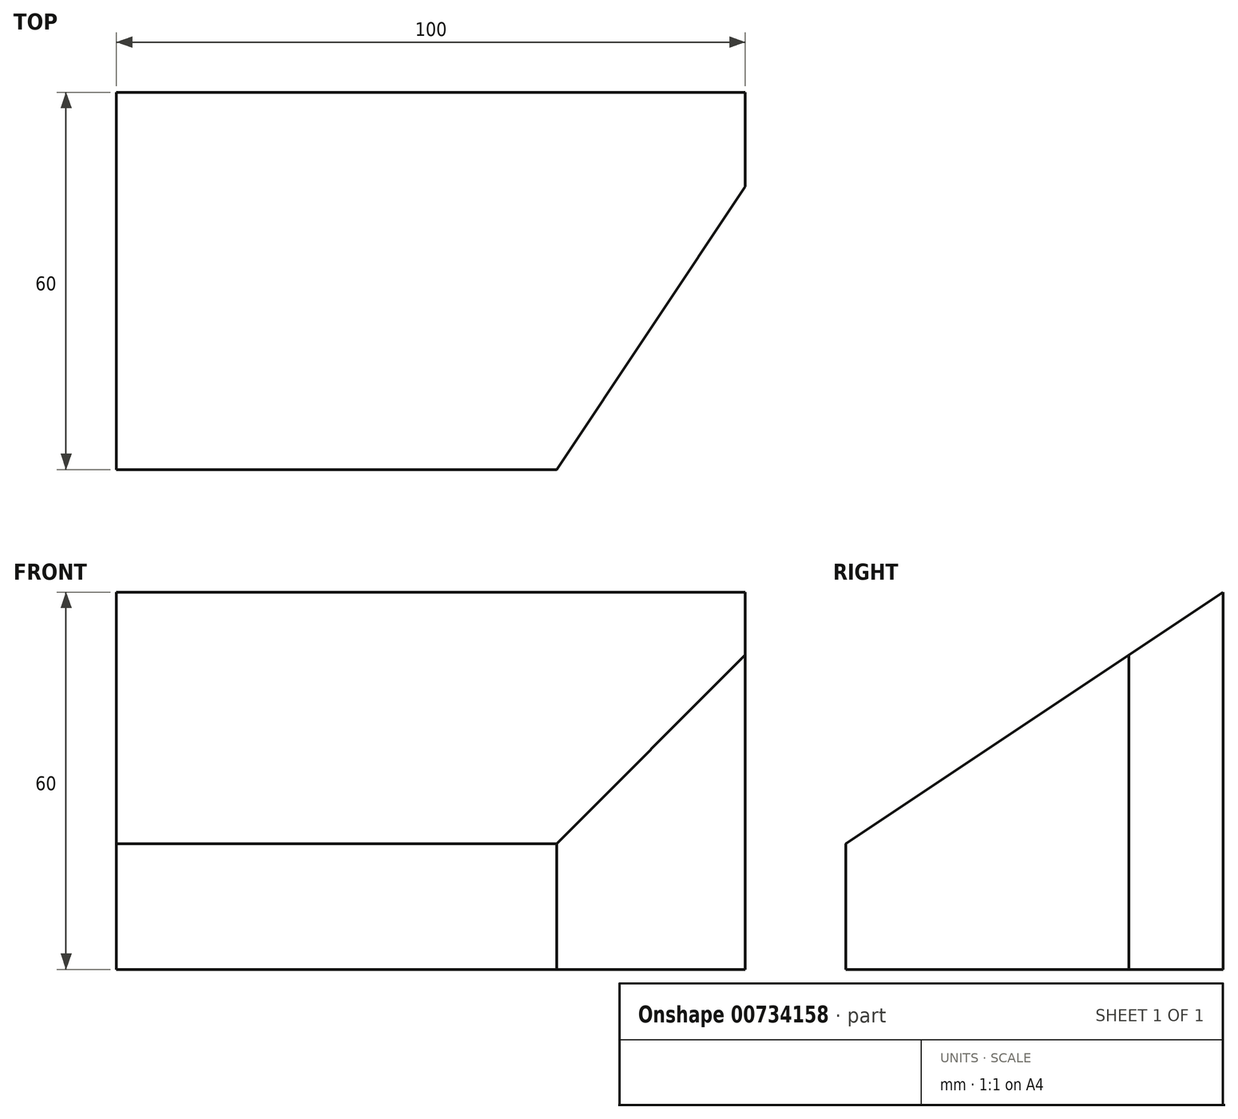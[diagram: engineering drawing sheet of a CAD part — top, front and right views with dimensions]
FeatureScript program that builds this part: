
annotation { "Feature Type Name" : "Feature", "Feature Type Description" : "" }
export const myFeature = defineFeature(function(context is Context, id is Id, definition is map)
    precondition{}
    {
        {
            var Q0;
            Q0=qCreatedBy(makeId("Top.planeOp"),FACE);
            var sketch = newSketch(context, id + "F0", { "sketchPlane" : qUnion([Q0])});
            skLineSegment(sketch, "E0", {"start": v(0, 0) * mm, "end": v(100, 0) * mm});
            skLineSegment(sketch, "E1", {"start": v(100, 0) * mm, "end": v(100, -60) * mm});
            skLineSegment(sketch, "E2", {"start": v(0, -60) * mm, "end": v(0, 0) * mm});
            skLineSegment(sketch, "E3", {"start": v(0, -60) * mm, "end": v(100, -60) * mm});
            skSolve(sketch);
        }
        {
            var Q0;
            Q0=makeQuery(id+"F0.imprint","IMPRINT",FACE,{"disambiguationData":[TD([[makeQuery(id+"F0.imprint","IMPRINT",EDGE,{"derivedFrom":sQuery(id+"F0.wireOp",EDGE,"E0")}),-1.0]])]});
            extrude(context, id + "F1", {"entities" : qUnion([Q0]), "depth" : 60 * mm, "offsetDistance" : 25 * mm});
        }
        {
            var Q0;
            Q0=makeQuery(id+"F1.opExtrude","CAP_FACE",FACE,{"disambiguationData":[OSD([sQuery(id+"F0.wireOp",EDGE,"E0"),sQuery(id+"F0.wireOp",EDGE,"E1"),sQuery(id+"F0.wireOp",EDGE,"E2"),sQuery(id+"F0.wireOp",EDGE,"E3")])],"isStart":false});
            var sketch = newSketch(context, id + "F2", { "sketchPlane" : qUnion([Q0])});
            skLineSegment(sketch, "E4", {"start": v(100, -15) * mm, "end": v(70, -60) * mm});
            skSolve(sketch);
        }
        {
            var Q0;
            {var subQ0=sQuery(id+"F2.wireOp",EDGE,"E4");Q0=makeQuery(id+"F2.imprint","IMPRINT",FACE,{"disambiguationData":[TD([[makeQuery(id+"F2.imprint","IMPRINT",EDGE,{"derivedFrom":subQ0}),1.0]])]});}
            var Q1;
            Q1=makeQuery(id+"F1.opExtrude","CAP_FACE",FACE,{"disambiguationData":[OSD([sQuery(id+"F0.wireOp",EDGE,"E0"),sQuery(id+"F0.wireOp",EDGE,"E1"),sQuery(id+"F0.wireOp",EDGE,"E2"),sQuery(id+"F0.wireOp",EDGE,"E3")])],"isStart":true});
            extrude(context, id + "F3", {"entities" : qUnion([Q0]), "operationType" : NewBodyOperationType.REMOVE, "endBound" : BoundingType.UP_TO_SURFACE, "oppositeDirection" : true, "depth" : 25 * mm, "endBoundEntityFace" : qUnion([Q1]), "offsetDistance" : 25 * mm});
        }
        {
            var Q0;
            Q0=makeQuery(id+"F1.opExtrude","SWEPT_FACE",FACE,{"disambiguationData":[OSD([sQuery(id+"F0.wireOp",EDGE,"E2")])]});
            var sketch = newSketch(context, id + "F4", { "sketchPlane" : qUnion([Q0])});
            skLineSegment(sketch, "E5", {"start": v(0, 60) * mm, "end": v(60, 20) * mm});
            skSolve(sketch);
        }
        {
            var Q0;
            {var subQ0=sQuery(id+"F4.wireOp",EDGE,"E5");Q0=makeQuery(id+"F4.imprint","IMPRINT",FACE,{"disambiguationData":[TD([[makeQuery(id+"F4.imprint","IMPRINT",EDGE,{"derivedFrom":subQ0}),1.0]])]});}
            var Q1;
            Q1=makeQuery(id+"F1.opExtrude","SWEPT_FACE",FACE,{"disambiguationData":[OSD([sQuery(id+"F0.wireOp",EDGE,"E1")])]});
            extrude(context, id + "F5", {"entities" : qUnion([Q0]), "operationType" : NewBodyOperationType.REMOVE, "endBound" : BoundingType.UP_TO_SURFACE, "oppositeDirection" : true, "depth" : 25 * mm, "endBoundEntityFace" : qUnion([Q1]), "offsetDistance" : 25 * mm});
        }
    });
